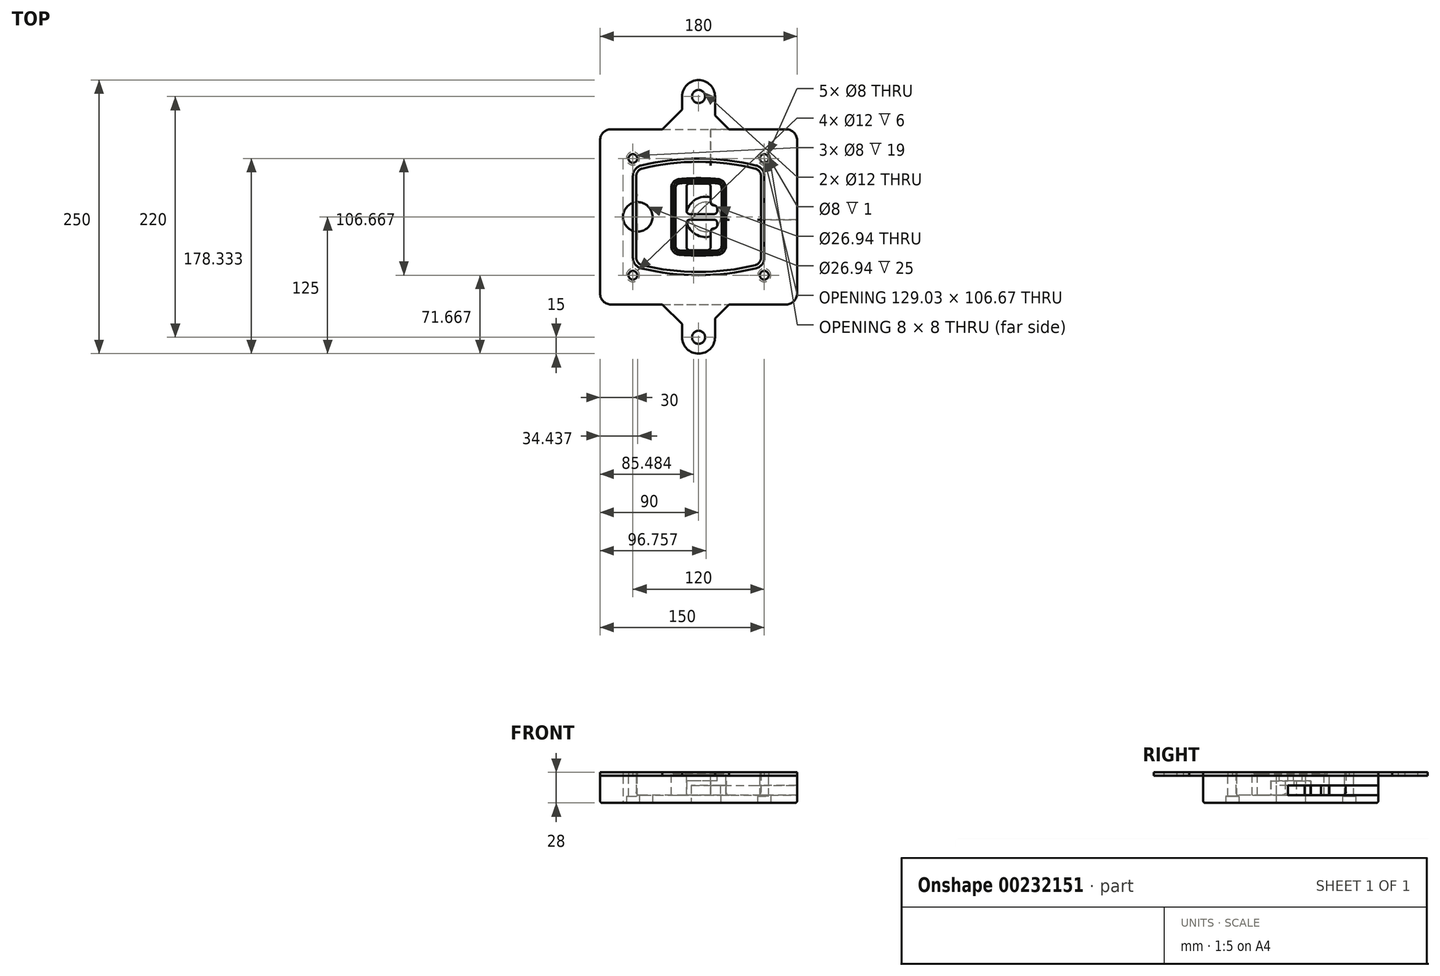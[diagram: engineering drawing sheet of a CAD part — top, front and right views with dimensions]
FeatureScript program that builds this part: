
annotation { "Feature Type Name" : "Feature", "Feature Type Description" : "" }
export const myFeature = defineFeature(function(context is Context, id is Id, definition is map)
    precondition{}
    {
        {
            var Q0;
            Q0=qCreatedBy(makeId("Top.planeOp"),FACE);
            var sketch = newSketch(context, id + "F0", { "sketchPlane" : qUnion([Q0])});
            skPoint(sketch, "E0.rect.middle", {"position": v(0, 0) * mm});
            skLineSegment(sketch, "E1.bottom", {"start": v(-80, -80) * mm, "end": v(80, -80) * mm});
            skLineSegment(sketch, "E1.top", {"start": v(-80, 80) * mm, "end": v(80, 80) * mm});
            skLineSegment(sketch, "E1.left", {"start": v(-90, -70) * mm, "end": v(-90, 70) * mm});
            skLineSegment(sketch, "E1.right", {"start": v(90, -70) * mm, "end": v(90, 70) * mm});
            skLineSegment(sketch, "E2", {"start": v(-90, 80) * mm, "end": v(90, -80) * mm, "construction": true});
            skLineSegment(sketch, "E3", {"start": v(90, 80) * mm, "end": v(-90, -80) * mm, "construction": true});
            skCircle(sketch, "E4", {"center": v(-60, 53.33) * mm, "radius": 4 * mm});
            skCircle(sketch, "E5", {"center": v(60, 53.33) * mm, "radius": 4 * mm});
            skCircle(sketch, "E6", {"center": v(60, -53.33) * mm, "radius": 4 * mm});
            skCircle(sketch, "E7", {"center": v(-60, -53.33) * mm, "radius": 4 * mm});
            skLineSegment(sketch, "E8", {"start": v(-60, 53.33) * mm, "end": v(60, 53.33) * mm, "construction": true});
            skLineSegment(sketch, "E9", {"start": v(60, 53.33) * mm, "end": v(60, -53.33) * mm, "construction": true});
            skLineSegment(sketch, "E10", {"start": v(60, -53.33) * mm, "end": v(-60, -53.33) * mm, "construction": true});
            skLineSegment(sketch, "E11", {"start": v(-60, -53.33) * mm, "end": v(-60, 53.33) * mm, "construction": true});
            skLineSegment(sketch, "E12", {"start": v(-60, 37.3) * mm, "end": v(-60, -37.3) * mm});
            skLineSegment(sketch, "E13", {"start": v(60, 37.3) * mm, "end": v(60, -37.3) * mm});
            skArc(sketch, "E14", {"start": v(52.38, 47.01) * mm, "mid": v(0, 53.33) * mm, "end": v(-52.38, 47.01) * mm});
            skArc(sketch, "E15", {"start": v(-52.38, -47.01) * mm, "mid": v(0, -53.33) * mm, "end": v(52.38, -47.01) * mm});
            skLineSegment(sketch, "E16", {"start": v(-60, 0) * mm, "end": v(60, 0) * mm, "construction": true});
            skPoint(sketch, "E17.visualSharp", {"position": v(-60, -45) * mm});
            skArc(sketch, "E17.filletArc", {"start": v(-60, -37.3) * mm, "mid": v(-57.87, -43.47) * mm, "end": v(-52.38, -47.01) * mm});
            skPoint(sketch, "E18.visualSharp", {"position": v(-60, 45) * mm});
            skArc(sketch, "E18.filletArc", {"start": v(-52.38, 47.01) * mm, "mid": v(-57.87, 43.47) * mm, "end": v(-60, 37.3) * mm});
            skPoint(sketch, "E19.visualSharp", {"position": v(60, 45) * mm});
            skArc(sketch, "E19.filletArc", {"start": v(60, 37.3) * mm, "mid": v(57.87, 43.47) * mm, "end": v(52.38, 47.01) * mm});
            skPoint(sketch, "E20.visualSharp", {"position": v(60, -45) * mm});
            skArc(sketch, "E20.filletArc", {"start": v(52.38, -47.01) * mm, "mid": v(57.87, -43.47) * mm, "end": v(60, -37.3) * mm});
            skPoint(sketch, "E21.visualSharp", {"position": v(-90, 80) * mm});
            skArc(sketch, "E21.filletArc", {"start": v(-80, 80) * mm, "mid": v(-87.07, 77.07) * mm, "end": v(-90, 70) * mm});
            skPoint(sketch, "E22.visualSharp", {"position": v(90, 80) * mm});
            skArc(sketch, "E22.filletArc", {"start": v(90, 70) * mm, "mid": v(87.07, 77.07) * mm, "end": v(80, 80) * mm});
            skPoint(sketch, "E23.visualSharp", {"position": v(90, -80) * mm});
            skArc(sketch, "E23.filletArc", {"start": v(80, -80) * mm, "mid": v(87.07, -77.07) * mm, "end": v(90, -70) * mm});
            skPoint(sketch, "E24.visualSharp", {"position": v(-90, -80) * mm});
            skArc(sketch, "E24.filletArc", {"start": v(-90, -70) * mm, "mid": v(-87.07, -77.07) * mm, "end": v(-80, -80) * mm});
            skArc(sketch, "E25.0", {"start": v(57, 37.3) * mm, "mid": v(55.5, 41.62) * mm, "end": v(51.67, 44.1) * mm});
            skLineSegment(sketch, "E25.1", {"start": v(57, 37.3) * mm, "end": v(57, -37.3) * mm});
            skArc(sketch, "E25.2", {"start": v(51.67, -44.1) * mm, "mid": v(55.5, -41.62) * mm, "end": v(57, -37.3) * mm});
            skArc(sketch, "E25.3", {"start": v(-51.67, -44.1) * mm, "mid": v(0, -50.33) * mm, "end": v(51.67, -44.1) * mm});
            skArc(sketch, "E25.4", {"start": v(-57, -37.3) * mm, "mid": v(-55.5, -41.62) * mm, "end": v(-51.67, -44.1) * mm});
            skArc(sketch, "E25.5", {"start": v(51.67, 44.1) * mm, "mid": v(0, 50.33) * mm, "end": v(-51.67, 44.1) * mm});
            skLineSegment(sketch, "E25.6", {"start": v(-57, 37.3) * mm, "end": v(-57, -37.3) * mm});
            skArc(sketch, "E25.7", {"start": v(-51.67, 44.1) * mm, "mid": v(-55.5, 41.62) * mm, "end": v(-57, 37.3) * mm});
            skArc(sketch, "E26.0", {"start": v(-53.33, 50.9) * mm, "mid": v(-61.01, 45.94) * mm, "end": v(-64, 37.3) * mm});
            skArc(sketch, "E26.1", {"start": v(53.33, 50.9) * mm, "mid": v(0, 57.33) * mm, "end": v(-53.33, 50.9) * mm});
            skArc(sketch, "E26.2", {"start": v(64, 37.3) * mm, "mid": v(61.01, 45.94) * mm, "end": v(53.33, 50.9) * mm});
            skLineSegment(sketch, "E26.3", {"start": v(64, 37.3) * mm, "end": v(64, -37.3) * mm});
            skArc(sketch, "E26.4", {"start": v(53.33, -50.9) * mm, "mid": v(61.01, -45.94) * mm, "end": v(64, -37.3) * mm});
            skLineSegment(sketch, "E26.5", {"start": v(-64, 37.3) * mm, "end": v(-64, -37.3) * mm});
            skArc(sketch, "E26.6", {"start": v(-53.33, -50.9) * mm, "mid": v(0, -57.33) * mm, "end": v(53.33, -50.9) * mm});
            skArc(sketch, "E26.7", {"start": v(-64, -37.3) * mm, "mid": v(-61.01, -45.94) * mm, "end": v(-53.33, -50.9) * mm});
            skSolve(sketch);
        }
        {
            var Q0;
            Q0=makeQuery(id+"F0.imprint","IMPRINT",FACE,{"disambiguationData":[TD([[makeQuery(id+"F0.imprint","IMPRINT",EDGE,{"derivedFrom":sQuery(id+"F0.wireOp",EDGE,"E1.bottom")}),1.0]])]});
            var Q1;
            Q1=makeQuery(id+"F0.imprint","IMPRINT",FACE,{"disambiguationData":[TD([[makeQuery(id+"F0.imprint","IMPRINT",EDGE,{"derivedFrom":sQuery(id+"F0.wireOp",EDGE,"E12")}),1.0]])]});
            var Q2;
            Q2=makeQuery(id+"F0.imprint","IMPRINT",FACE,{"disambiguationData":[TD([[makeQuery(id+"F0.imprint","IMPRINT",EDGE,{"derivedFrom":sQuery(id+"F0.wireOp",EDGE,"E25.0")}),1.0]])]});
            var Q3;
            Q3=makeQuery(id+"F0.imprint","IMPRINT",FACE,{"disambiguationData":[TD([[makeQuery(id+"F0.imprint","IMPRINT",EDGE,{"derivedFrom":sQuery(id+"F0.wireOp",EDGE,"E12")}),-1.0]])]});
            extrude(context, id + "F1", {"entities" : qUnion([Q0, Q1, Q2, Q3]), "oppositeDirection" : true, "depth" : 25 * mm});
        }
        {
            var Q0;
            Q0=makeQuery(id+"F0.imprint","IMPRINT",FACE,{"disambiguationData":[TD([[makeQuery(id+"F0.imprint","IMPRINT",EDGE,{"derivedFrom":sQuery(id+"F0.wireOp",EDGE,"E12")}),1.0]])]});
            extrude(context, id + "F2", {"entities" : qUnion([Q0]), "operationType" : NewBodyOperationType.ADD, "depth" : 3 * mm});
        }
        {
            var Q0;
            Q0=makeQuery(id+"F0.imprint","IMPRINT",FACE,{"disambiguationData":[TD([[makeQuery(id+"F0.imprint","IMPRINT",EDGE,{"derivedFrom":sQuery(id+"F0.wireOp",EDGE,"E25.0")}),1.0]])]});
            extrude(context, id + "F3", {"entities" : qUnion([Q0]), "operationType" : NewBodyOperationType.REMOVE, "oppositeDirection" : true, "depth" : 18 * mm});
        }
        {
            var Q0;
            Q0=makeQuery(id+"F2.opExtrude","CAP_FACE",FACE,{"disambiguationData":[OSD([sQuery(id+"F0.wireOp",EDGE,"E12"),sQuery(id+"F0.wireOp",EDGE,"E13"),sQuery(id+"F0.wireOp",EDGE,"E14"),sQuery(id+"F0.wireOp",EDGE,"E15"),sQuery(id+"F0.wireOp",EDGE,"E17.filletArc"),sQuery(id+"F0.wireOp",EDGE,"E18.filletArc"),sQuery(id+"F0.wireOp",EDGE,"E19.filletArc"),sQuery(id+"F0.wireOp",EDGE,"E20.filletArc"),sQuery(id+"F0.wireOp",EDGE,"E25.0"),sQuery(id+"F0.wireOp",EDGE,"E25.1"),sQuery(id+"F0.wireOp",EDGE,"E25.2"),sQuery(id+"F0.wireOp",EDGE,"E25.3"),sQuery(id+"F0.wireOp",EDGE,"E25.4"),sQuery(id+"F0.wireOp",EDGE,"E25.5"),sQuery(id+"F0.wireOp",EDGE,"E25.6"),sQuery(id+"F0.wireOp",EDGE,"E25.7")])],"isStart":false});
            var sketch = newSketch(context, id + "F4", { "sketchPlane" : qUnion([Q0])});
            skArc(sketch, "E27.0", {"start": v(-17.7, -34.56) * mm, "mid": v(0, -35.33) * mm, "end": v(17.7, -34.56) * mm});
            skArc(sketch, "E28.0", {"start": v(17.7, 34.56) * mm, "mid": v(0, 35.33) * mm, "end": v(-17.7, 34.56) * mm});
            skLineSegment(sketch, "E29", {"start": v(-25, 26.59) * mm, "end": v(-25, -26.59) * mm});
            skLineSegment(sketch, "E30", {"start": v(25, 26.59) * mm, "end": v(25, -26.59) * mm});
            skLineSegment(sketch, "E31", {"start": v(-25, 33.78) * mm, "end": v(25, 33.78) * mm, "construction": true});
            skLineSegment(sketch, "E32", {"start": v(-25, -33.78) * mm, "end": v(25, -33.78) * mm, "construction": true});
            skPoint(sketch, "E33.visualSharp", {"position": v(-25, 33.78) * mm});
            skArc(sketch, "E33.filletArc", {"start": v(-17.7, 34.56) * mm, "mid": v(-22.9, 32) * mm, "end": v(-25, 26.59) * mm});
            skPoint(sketch, "E34.visualSharp", {"position": v(25, 33.78) * mm});
            skArc(sketch, "E34.filletArc", {"start": v(25, 26.59) * mm, "mid": v(22.9, 32) * mm, "end": v(17.7, 34.56) * mm});
            skPoint(sketch, "E35.visualSharp", {"position": v(25, -33.78) * mm});
            skArc(sketch, "E35.filletArc", {"start": v(17.7, -34.56) * mm, "mid": v(22.9, -32) * mm, "end": v(25, -26.59) * mm});
            skPoint(sketch, "E36.visualSharp", {"position": v(-25, -33.78) * mm});
            skArc(sketch, "E36.filletArc", {"start": v(-25, -26.59) * mm, "mid": v(-22.9, -32) * mm, "end": v(-17.7, -34.56) * mm});
            skArc(sketch, "E37.0", {"start": v(51.67, 44.1) * mm, "mid": v(0, 50.33) * mm, "end": v(-51.67, 44.1) * mm});
            skArc(sketch, "E37.1", {"start": v(-51.67, 44.1) * mm, "mid": v(-55.5, 41.62) * mm, "end": v(-57, 37.3) * mm});
            skLineSegment(sketch, "E37.2", {"start": v(-57, 37.3) * mm, "end": v(-57, -37.3) * mm});
            skArc(sketch, "E37.3", {"start": v(-57, -37.3) * mm, "mid": v(-55.5, -41.62) * mm, "end": v(-51.67, -44.1) * mm});
            skArc(sketch, "E37.4", {"start": v(-51.67, -44.1) * mm, "mid": v(0, -50.33) * mm, "end": v(51.67, -44.1) * mm});
            skArc(sketch, "E37.5", {"start": v(51.67, -44.1) * mm, "mid": v(55.5, -41.62) * mm, "end": v(57, -37.3) * mm});
            skLineSegment(sketch, "E37.6", {"start": v(57, 37.3) * mm, "end": v(57, -37.3) * mm});
            skArc(sketch, "E37.7", {"start": v(57, 37.3) * mm, "mid": v(55.5, 41.62) * mm, "end": v(51.67, 44.1) * mm});
            skLineSegment(sketch, "E38.0", {"start": v(23, 26.59) * mm, "end": v(23, -26.59) * mm});
            skArc(sketch, "E38.1", {"start": v(17.53, -32.56) * mm, "mid": v(21.42, -30.64) * mm, "end": v(23, -26.59) * mm});
            skArc(sketch, "E38.2", {"start": v(-17.53, -32.56) * mm, "mid": v(0, -33.33) * mm, "end": v(17.53, -32.56) * mm});
            skArc(sketch, "E38.3", {"start": v(-23, -26.59) * mm, "mid": v(-21.42, -30.64) * mm, "end": v(-17.53, -32.56) * mm});
            skLineSegment(sketch, "E38.4", {"start": v(-23, 26.59) * mm, "end": v(-23, -26.59) * mm});
            skArc(sketch, "E38.5", {"start": v(23, 26.59) * mm, "mid": v(21.42, 30.64) * mm, "end": v(17.53, 32.56) * mm});
            skArc(sketch, "E38.6", {"start": v(-17.53, 32.56) * mm, "mid": v(-21.42, 30.64) * mm, "end": v(-23, 26.59) * mm});
            skArc(sketch, "E38.7", {"start": v(17.53, 32.56) * mm, "mid": v(0, 33.33) * mm, "end": v(-17.53, 32.56) * mm});
            skArc(sketch, "E39.0", {"start": v(21, 26.59) * mm, "mid": v(19.95, 29.29) * mm, "end": v(17.35, 30.57) * mm});
            skLineSegment(sketch, "E39.1", {"start": v(21, 26.59) * mm, "end": v(21, -26.59) * mm});
            skArc(sketch, "E39.2", {"start": v(17.35, -30.57) * mm, "mid": v(19.95, -29.29) * mm, "end": v(21, -26.59) * mm});
            skArc(sketch, "E39.3", {"start": v(-17.35, -30.57) * mm, "mid": v(0, -31.33) * mm, "end": v(17.35, -30.57) * mm});
            skArc(sketch, "E39.4", {"start": v(-21, -26.59) * mm, "mid": v(-19.95, -29.29) * mm, "end": v(-17.35, -30.57) * mm});
            skArc(sketch, "E39.5", {"start": v(17.35, 30.57) * mm, "mid": v(0, 31.33) * mm, "end": v(-17.35, 30.57) * mm});
            skLineSegment(sketch, "E39.6", {"start": v(-21, 26.59) * mm, "end": v(-21, -26.59) * mm});
            skArc(sketch, "E39.7", {"start": v(-17.35, 30.57) * mm, "mid": v(-19.95, 29.29) * mm, "end": v(-21, 26.59) * mm});
            skLineSegment(sketch, "E40", {"start": v(-25, 0) * mm, "end": v(25, 0) * mm, "construction": true});
            skLineSegment(sketch, "E41", {"start": v(-11, 5.5) * mm, "end": v(-11, 27.5) * mm});
            skLineSegment(sketch, "E42", {"start": v(-8, 30.5) * mm, "end": v(8, 30.5) * mm});
            skLineSegment(sketch, "E43", {"start": v(11, 27.5) * mm, "end": v(11, 13.5) * mm});
            skLineSegment(sketch, "E44", {"start": v(14, 10.5) * mm, "end": v(14, 10.5) * mm});
            skLineSegment(sketch, "E45", {"start": v(17, 7.5) * mm, "end": v(17, 5.5) * mm});
            skLineSegment(sketch, "E46", {"start": v(14, 2.5) * mm, "end": v(-8, 2.5) * mm});
            skPoint(sketch, "E47.visualSharp", {"position": v(-11, 30.5) * mm});
            skArc(sketch, "E47.filletArc", {"start": v(-8, 30.5) * mm, "mid": v(-10.12, 29.62) * mm, "end": v(-11, 27.5) * mm});
            skPoint(sketch, "E48.visualSharp", {"position": v(11, 30.5) * mm});
            skArc(sketch, "E48.filletArc", {"start": v(11, 27.5) * mm, "mid": v(10.12, 29.62) * mm, "end": v(8, 30.5) * mm});
            skPoint(sketch, "E49.visualSharp", {"position": v(11, 10.5) * mm});
            skArc(sketch, "E49.filletArc", {"start": v(11, 13.5) * mm, "mid": v(11.88, 11.38) * mm, "end": v(14, 10.5) * mm});
            skPoint(sketch, "E50.visualSharp", {"position": v(17, 10.5) * mm});
            skArc(sketch, "E50.filletArc", {"start": v(17, 7.5) * mm, "mid": v(16.12, 9.62) * mm, "end": v(14, 10.5) * mm});
            skPoint(sketch, "E51.visualSharp", {"position": v(17, 2.5) * mm});
            skArc(sketch, "E51.filletArc", {"start": v(14, 2.5) * mm, "mid": v(16.12, 3.38) * mm, "end": v(17, 5.5) * mm});
            skPoint(sketch, "E52.visualSharp", {"position": v(-11, 2.5) * mm});
            skArc(sketch, "E52.filletArc", {"start": v(-11, 5.5) * mm, "mid": v(-10.12, 3.38) * mm, "end": v(-8, 2.5) * mm});
            skLineSegment(sketch, "E53.0.MirrorCS", {"start": v(14, -2.5) * mm, "end": v(-8, -2.5) * mm});
            skArc(sketch, "E54.0.MirrorCS", {"start": v(-11, -5.5) * mm, "mid": v(-10.12, -3.38) * mm, "end": v(-8, -2.5) * mm});
            skLineSegment(sketch, "E55.0.MirrorCS", {"start": v(-11, -5.5) * mm, "end": v(-11, -27.5) * mm});
            skArc(sketch, "E56.0.MirrorCS", {"start": v(-8, -30.5) * mm, "mid": v(-10.12, -29.62) * mm, "end": v(-11, -27.5) * mm});
            skLineSegment(sketch, "E57.0.MirrorCS", {"start": v(-8, -30.5) * mm, "end": v(8, -30.5) * mm});
            skArc(sketch, "E58.0.MirrorCS", {"start": v(11, -27.5) * mm, "mid": v(10.12, -29.62) * mm, "end": v(8, -30.5) * mm});
            skLineSegment(sketch, "E59.0.MirrorCS", {"start": v(11, -27.5) * mm, "end": v(11, -13.5) * mm});
            skArc(sketch, "E60.0.MirrorCS", {"start": v(11, -13.5) * mm, "mid": v(11.88, -11.38) * mm, "end": v(14, -10.5) * mm});
            skArc(sketch, "E61.0.MirrorCS", {"start": v(17, -7.5) * mm, "mid": v(16.12, -9.62) * mm, "end": v(14, -10.5) * mm});
            skLineSegment(sketch, "E62.0.MirrorCS", {"start": v(17, -7.5) * mm, "end": v(17, -5.5) * mm});
            skArc(sketch, "E63.0.MirrorCS", {"start": v(14, -2.5) * mm, "mid": v(16.12, -3.38) * mm, "end": v(17, -5.5) * mm});
            skSolve(sketch);
        }
        {
            var Q0;
            Q0=makeQuery(id+"F4.imprint","IMPRINT",FACE,{"disambiguationData":[TD([[makeQuery(id+"F4.imprint","IMPRINT",EDGE,{"derivedFrom":sQuery(id+"F4.wireOp",EDGE,"E27.0")}),1.0]])]});
            var Q1;
            Q1=makeQuery(id+"F4.imprint","IMPRINT",FACE,{"disambiguationData":[TD([[makeQuery(id+"F4.imprint","IMPRINT",EDGE,{"derivedFrom":sQuery(id+"F4.wireOp",EDGE,"E38.0")}),-1.0]])]});
            var Q2;
            Q2=makeQuery(id+"F4.imprint","IMPRINT",FACE,{"disambiguationData":[TD([[makeQuery(id+"F4.imprint","IMPRINT",EDGE,{"derivedFrom":sQuery(id+"F4.wireOp",EDGE,"E39.0")}),1.0]])]});
            extrude(context, id + "F5", {"entities" : qUnion([Q0, Q1, Q2]), "operationType" : NewBodyOperationType.ADD, "endBound" : BoundingType.UP_TO_NEXT, "oppositeDirection" : true, "depth" : 25 * mm});
        }
        {
            var Q0;
            Q0=makeQuery(id+"F4.imprint","IMPRINT",FACE,{"disambiguationData":[TD([[makeQuery(id+"F4.imprint","IMPRINT",EDGE,{"derivedFrom":sQuery(id+"F4.wireOp",EDGE,"E38.0")}),-1.0]])]});
            extrude(context, id + "F6", {"entities" : qUnion([Q0]), "operationType" : NewBodyOperationType.REMOVE, "oppositeDirection" : true, "depth" : 2 * mm});
        }
        {
            var Q0;
            Q0=makeQuery(id+"F1.opExtrude","CAP_FACE",FACE,{"disambiguationData":[OSD([sQuery(id+"F0.wireOp",EDGE,"E1.bottom"),sQuery(id+"F0.wireOp",EDGE,"E1.top"),sQuery(id+"F0.wireOp",EDGE,"E1.left"),sQuery(id+"F0.wireOp",EDGE,"E1.right"),sQuery(id+"F0.wireOp",EDGE,"E4"),sQuery(id+"F0.wireOp",EDGE,"E5"),sQuery(id+"F0.wireOp",EDGE,"E6"),sQuery(id+"F0.wireOp",EDGE,"E7"),sQuery(id+"F0.wireOp",EDGE,"E21.filletArc"),sQuery(id+"F0.wireOp",EDGE,"E22.filletArc"),sQuery(id+"F0.wireOp",EDGE,"E23.filletArc"),sQuery(id+"F0.wireOp",EDGE,"E24.filletArc")])],"isStart":false});
            var sketch = newSketch(context, id + "F7", { "sketchPlane" : qUnion([Q0])});
            skCircle(sketch, "E64", {"center": v(6.76, 0) * mm, "radius": 13.47 * mm});
            skCircle(sketch, "E65", {"center": v(-55.56, 0) * mm, "radius": 13.47 * mm});
            skLineSegment(sketch, "E66", {"start": v(90, 0) * mm, "end": v(-90, 0) * mm});
            skCircle(sketch, "E67", {"center": v(6.76, 0) * mm, "radius": 18.47 * mm});
            skCircle(sketch, "E68", {"center": v(60, -53.33) * mm, "radius": 6 * mm});
            skCircle(sketch, "E69", {"center": v(-60, -53.33) * mm, "radius": 6 * mm});
            skCircle(sketch, "E70", {"center": v(-60, 53.33) * mm, "radius": 6 * mm});
            skCircle(sketch, "E71", {"center": v(60, 53.33) * mm, "radius": 6 * mm});
            skSolve(sketch);
        }
        {
            var Q0;
            {var subQ1=sQuery(id+"F7.wireOp",EDGE,"E66");var subQ4=sQuery(id+"F7.wireOp",EDGE,"E64");var subQ6=makeQuery(id+"F7.imprint","INTERSECT",VERTEX,{"disambiguationData":[OD(0.0)],"derivedFrom":[subQ4,subQ1]});Q0=makeQuery(id+"F7.imprint","IMPRINT",FACE,{"disambiguationData":[TD([[makeQuery(id+"F7.imprint","IMPRINT",EDGE,{"disambiguationData":[TD([[subQ6,-1.0]])],"derivedFrom":subQ4}),-1.0]])]});}
            var Q1;
            {var subQ0=sQuery(id+"F7.wireOp",EDGE,"E66");var subQ1=sQuery(id+"F7.wireOp",EDGE,"E64");var subQ3=makeQuery(id+"F7.imprint","INTERSECT",VERTEX,{"disambiguationData":[OD(0.0)],"derivedFrom":[subQ1,subQ0]});Q1=makeQuery(id+"F7.imprint","IMPRINT",FACE,{"disambiguationData":[TD([[makeQuery(id+"F7.imprint","IMPRINT",EDGE,{"disambiguationData":[TD([[subQ3,-1.0]])],"derivedFrom":subQ1}),1.0]])]});}
            var Q2;
            {var subQ0=sQuery(id+"F7.wireOp",EDGE,"E66");var subQ1=sQuery(id+"F7.wireOp",EDGE,"E64");var subQ3=makeQuery(id+"F7.imprint","INTERSECT",VERTEX,{"disambiguationData":[OD(0.0)],"derivedFrom":[subQ1,subQ0]});Q2=makeQuery(id+"F7.imprint","IMPRINT",FACE,{"disambiguationData":[TD([[makeQuery(id+"F7.imprint","IMPRINT",EDGE,{"disambiguationData":[TD([[subQ3,1.0]])],"derivedFrom":subQ1}),1.0]])]});}
            var Q3;
            {var subQ1=sQuery(id+"F7.wireOp",EDGE,"E66");var subQ4=sQuery(id+"F7.wireOp",EDGE,"E64");var subQ6=makeQuery(id+"F7.imprint","INTERSECT",VERTEX,{"disambiguationData":[OD(0.0)],"derivedFrom":[subQ4,subQ1]});Q3=makeQuery(id+"F7.imprint","IMPRINT",FACE,{"disambiguationData":[TD([[makeQuery(id+"F7.imprint","IMPRINT",EDGE,{"disambiguationData":[TD([[subQ6,1.0]])],"derivedFrom":subQ4}),-1.0]])]});}
            extrude(context, id + "F8", {"entities" : qUnion([Q0, Q1, Q2, Q3]), "operationType" : NewBodyOperationType.ADD, "oppositeDirection" : true, "depth" : 20 * mm});
        }
        {
            var Q0;
            {var subQ0=sQuery(id+"F7.wireOp",EDGE,"E66");var subQ1=sQuery(id+"F7.wireOp",EDGE,"E64");var subQ3=makeQuery(id+"F7.imprint","INTERSECT",VERTEX,{"disambiguationData":[OD(0.0)],"derivedFrom":[subQ1,subQ0]});Q0=makeQuery(id+"F7.imprint","IMPRINT",FACE,{"disambiguationData":[TD([[makeQuery(id+"F7.imprint","IMPRINT",EDGE,{"disambiguationData":[TD([[subQ3,-1.0]])],"derivedFrom":subQ1}),1.0]])]});}
            var Q1;
            {var subQ0=sQuery(id+"F7.wireOp",EDGE,"E66");var subQ1=sQuery(id+"F7.wireOp",EDGE,"E64");var subQ3=makeQuery(id+"F7.imprint","INTERSECT",VERTEX,{"disambiguationData":[OD(0.0)],"derivedFrom":[subQ1,subQ0]});Q1=makeQuery(id+"F7.imprint","IMPRINT",FACE,{"disambiguationData":[TD([[makeQuery(id+"F7.imprint","IMPRINT",EDGE,{"disambiguationData":[TD([[subQ3,1.0]])],"derivedFrom":subQ1}),1.0]])]});}
            extrude(context, id + "F9", {"entities" : qUnion([Q0, Q1]), "operationType" : NewBodyOperationType.REMOVE, "oppositeDirection" : true, "depth" : 16 * mm});
        }
        {
            var Q0;
            {var subQ0=sQuery(id+"F7.wireOp",EDGE,"E66");var subQ1=sQuery(id+"F7.wireOp",EDGE,"E65");var subQ3=makeQuery(id+"F7.imprint","INTERSECT",VERTEX,{"disambiguationData":[OD(0.0)],"derivedFrom":[subQ1,subQ0]});Q0=makeQuery(id+"F7.imprint","IMPRINT",FACE,{"disambiguationData":[TD([[makeQuery(id+"F7.imprint","IMPRINT",EDGE,{"disambiguationData":[TD([[subQ3,-1.0]])],"derivedFrom":subQ1}),1.0]])]});}
            var Q1;
            {var subQ0=sQuery(id+"F7.wireOp",EDGE,"E66");var subQ1=sQuery(id+"F7.wireOp",EDGE,"E65");var subQ3=makeQuery(id+"F7.imprint","INTERSECT",VERTEX,{"disambiguationData":[OD(0.0)],"derivedFrom":[subQ1,subQ0]});Q1=makeQuery(id+"F7.imprint","IMPRINT",FACE,{"disambiguationData":[TD([[makeQuery(id+"F7.imprint","IMPRINT",EDGE,{"disambiguationData":[TD([[subQ3,1.0]])],"derivedFrom":subQ1}),1.0]])]});}
            extrude(context, id + "F10", {"entities" : qUnion([Q0, Q1]), "operationType" : NewBodyOperationType.REMOVE, "oppositeDirection" : true, "depth" : 25 * mm});
        }
        {
            var Q0;
            Q0=makeQuery(id+"F7.imprint","IMPRINT",FACE,{"disambiguationData":[TD([[makeQuery(id+"F7.imprint","IMPRINT",EDGE,{"derivedFrom":sQuery(id+"F7.wireOp",EDGE,"E68")}),1.0]])]});
            var Q1;
            Q1=makeQuery(id+"F7.imprint","IMPRINT",FACE,{"disambiguationData":[TD([[makeQuery(id+"F7.imprint","IMPRINT",EDGE,{"derivedFrom":makeQuery(id+"F1.opExtrude","CAP_EDGE",EDGE,{"disambiguationData":[OSD([sQuery(id+"F0.wireOp",EDGE,"E5")])],"isStart":false})}),-1.0]])]});
            var Q2;
            Q2=makeQuery(id+"F7.imprint","IMPRINT",FACE,{"disambiguationData":[TD([[makeQuery(id+"F7.imprint","IMPRINT",EDGE,{"derivedFrom":sQuery(id+"F7.wireOp",EDGE,"E69")}),1.0]])]});
            var Q3;
            Q3=makeQuery(id+"F7.imprint","IMPRINT",FACE,{"disambiguationData":[TD([[makeQuery(id+"F7.imprint","IMPRINT",EDGE,{"derivedFrom":makeQuery(id+"F1.opExtrude","CAP_EDGE",EDGE,{"disambiguationData":[OSD([sQuery(id+"F0.wireOp",EDGE,"E4")])],"isStart":false})}),-1.0]])]});
            var Q4;
            Q4=makeQuery(id+"F7.imprint","IMPRINT",FACE,{"disambiguationData":[TD([[makeQuery(id+"F7.imprint","IMPRINT",EDGE,{"derivedFrom":sQuery(id+"F7.wireOp",EDGE,"E70")}),1.0]])]});
            var Q5;
            Q5=makeQuery(id+"F7.imprint","IMPRINT",FACE,{"disambiguationData":[TD([[makeQuery(id+"F7.imprint","IMPRINT",EDGE,{"derivedFrom":makeQuery(id+"F1.opExtrude","CAP_EDGE",EDGE,{"disambiguationData":[OSD([sQuery(id+"F0.wireOp",EDGE,"E7")])],"isStart":false})}),-1.0]])]});
            var Q6;
            Q6=makeQuery(id+"F7.imprint","IMPRINT",FACE,{"disambiguationData":[TD([[makeQuery(id+"F7.imprint","IMPRINT",EDGE,{"derivedFrom":sQuery(id+"F7.wireOp",EDGE,"E71")}),1.0]])]});
            var Q7;
            Q7=makeQuery(id+"F7.imprint","IMPRINT",FACE,{"disambiguationData":[TD([[makeQuery(id+"F7.imprint","IMPRINT",EDGE,{"derivedFrom":makeQuery(id+"F1.opExtrude","CAP_EDGE",EDGE,{"disambiguationData":[OSD([sQuery(id+"F0.wireOp",EDGE,"E6")])],"isStart":false})}),-1.0]])]});
            extrude(context, id + "F11", {"entities" : qUnion([Q0, Q1, Q2, Q3, Q4, Q5, Q6, Q7]), "operationType" : NewBodyOperationType.REMOVE, "oppositeDirection" : true, "depth" : 6 * mm});
        }
        {
            var Q0;
            Q0=makeQuery(id+"F9.boolean.opBoolean","COPY",FACE,{"derivedFrom":makeQuery(id+"F9.opExtrude","CAP_FACE",FACE,{"disambiguationData":[OSD([sQuery(id+"F7.wireOp",EDGE,"E64")])],"isStart":false})});
            var sketch = newSketch(context, id + "F12", { "sketchPlane" : qUnion([Q0])});
            skArc(sketch, "E72.0", {"start": v(11, -88.19) * mm, "mid": v(97.1, -83.6) * mm, "end": v(92.5, 2.5) * mm});
            skLineSegment(sketch, "E72.1", {"start": v(11, -17.97) * mm, "end": v(11, -17.97) * mm});
            skLineSegment(sketch, "E73", {"start": v(92.5, -105.13) * mm, "end": v(102.3, -105.13) * mm});
            skLineSegment(sketch, "E74.0", {"start": v(92.5, 2.5) * mm, "end": v(14, 2.5) * mm});
            skArc(sketch, "E74.1", {"start": v(14, 2.5) * mm, "mid": v(16.12, 3.38) * mm, "end": v(17, 5.5) * mm});
            skLineSegment(sketch, "E74.2", {"start": v(17, 7.5) * mm, "end": v(17, 5.5) * mm});
            skArc(sketch, "E74.3", {"start": v(17, 7.5) * mm, "mid": v(16.12, 9.62) * mm, "end": v(14, 10.5) * mm});
            skArc(sketch, "E74.4", {"start": v(11, 13.5) * mm, "mid": v(11.88, 11.38) * mm, "end": v(14, 10.5) * mm});
            skLineSegment(sketch, "E74.5", {"start": v(11, 13.5) * mm, "end": v(11, -88.19) * mm});
            skLineSegment(sketch, "E74.7", {"start": v(92.5, -2.5) * mm, "end": v(14, -2.5) * mm});
            skArc(sketch, "E74.8", {"start": v(14, -2.5) * mm, "mid": v(16.12, -3.38) * mm, "end": v(17, -5.5) * mm});
            skLineSegment(sketch, "E74.9", {"start": v(17, -7.5) * mm, "end": v(17, -5.5) * mm});
            skArc(sketch, "E74.10", {"start": v(17, -7.5) * mm, "mid": v(16.12, -9.62) * mm, "end": v(14, -10.5) * mm});
            skArc(sketch, "E74.11", {"start": v(11, -13.5) * mm, "mid": v(11.88, -11.38) * mm, "end": v(14, -10.5) * mm});
            skLineSegment(sketch, "E74.12", {"start": v(11, -17.97) * mm, "end": v(11, -13.5) * mm});
            skPoint(sketch, "E75.orphan", {"position": v(11, -27.5) * mm});
            skPoint(sketch, "E76.orphan", {"position": v(-8, -2.5) * mm});
            skPoint(sketch, "E77.orphan", {"position": v(-8, 2.5) * mm});
            skPoint(sketch, "E78.orphan", {"position": v(11, 27.5) * mm});
            skSolve(sketch);
        }
        {
            var Q0;
            {var subQ7=sQuery(id+"F12.wireOp",EDGE,"E72.0");var subQ14=sQuery(id+"F12.wireOp",EDGE,"E72.1");var subQ16=sQuery(id+"F12.wireOp",EDGE,"E74.1");var subQ18=sQuery(id+"F12.wireOp",EDGE,"E74.8");Q0=qUnion([makeQuery(id+"F12.imprint","IMPRINT",FACE,{"disambiguationData":[TD([[makeQuery(id+"F12.imprint","IMPRINT",EDGE,{"derivedFrom":subQ7}),1.0]])]}),makeQuery(id+"F12.imprint","IMPRINT",FACE,{"disambiguationData":[TD([[makeQuery(id+"F12.imprint","IMPRINT",EDGE,{"derivedFrom":subQ14}),1.0]])]}),makeQuery(id+"F12.imprint","IMPRINT",FACE,{"disambiguationData":[TD([[makeQuery(id+"F12.imprint","IMPRINT",EDGE,{"derivedFrom":subQ16}),1.0]])]}),makeQuery(id+"F12.imprint","IMPRINT",FACE,{"disambiguationData":[TD([[makeQuery(id+"F12.imprint","IMPRINT",EDGE,{"derivedFrom":subQ18}),-1.0]])]})]);}
            var Q1;
            Q1=makeQuery(id+"F5.boolean.opBoolean","SPLIT",FACE,{"disambiguationData":[TD([makeQuery(id+"F5.opExtrude","SWEPT_FACE",FACE,{"disambiguationData":[OSD([sQuery(id+"F4.wireOp",EDGE,"E41")])]})])],"derivedFrom":makeQuery(id+"F3.boolean.opBoolean","COPY",FACE,{"derivedFrom":makeQuery(id+"F3.opExtrude","CAP_FACE",FACE,{"disambiguationData":[OSD([sQuery(id+"F0.wireOp",EDGE,"E25.0"),sQuery(id+"F0.wireOp",EDGE,"E25.1"),sQuery(id+"F0.wireOp",EDGE,"E25.2"),sQuery(id+"F0.wireOp",EDGE,"E25.3"),sQuery(id+"F0.wireOp",EDGE,"E25.4"),sQuery(id+"F0.wireOp",EDGE,"E25.5"),sQuery(id+"F0.wireOp",EDGE,"E25.6"),sQuery(id+"F0.wireOp",EDGE,"E25.7")])],"isStart":false})})});
            extrude(context, id + "F13", {"entities" : qUnion([Q0]), "operationType" : NewBodyOperationType.REMOVE, "endBound" : BoundingType.UP_TO_SURFACE, "endBoundEntityFace" : qUnion([Q1]), "depth" : 25 * mm});
        }
        {
            var Q0;
            Q0=makeQuery(id+"F3.boolean.opBoolean","COPY",EDGE,{"derivedFrom":makeQuery(id+"F3.opExtrude","CAP_EDGE",EDGE,{"disambiguationData":[OSD([sQuery(id+"F0.wireOp",EDGE,"E25.6")])],"isStart":false})});
            var Q1;
            Q1=makeQuery(id+"F8.boolean.opBoolean","INTERSECT",EDGE,{"derivedFrom":[makeQuery(id+"F5.opExtrude","SWEPT_FACE",FACE,{"disambiguationData":[OSD([sQuery(id+"F4.wireOp",EDGE,"E30")])]}),makeQuery(id+"F8.opExtrude","CAP_FACE",FACE,{"disambiguationData":[OSD([sQuery(id+"F7.wireOp",EDGE,"E67")])],"isStart":false})]});
            var Q2;
            Q2=makeQuery(id+"F8.boolean.opBoolean","INTERSECT",EDGE,{"disambiguationData":[OD(1.0)],"derivedFrom":[makeQuery(id+"F5.opExtrude","SWEPT_FACE",FACE,{"disambiguationData":[OSD([sQuery(id+"F4.wireOp",EDGE,"E30")])]}),makeQuery(id+"F8.opExtrude","SWEPT_FACE",FACE,{"disambiguationData":[OSD([sQuery(id+"F7.wireOp",EDGE,"E67")])]})]});
            var Q3;
            {var subQ0=makeQuery(id+"F3.boolean.opBoolean","COPY",FACE,{"derivedFrom":makeQuery(id+"F3.opExtrude","CAP_FACE",FACE,{"disambiguationData":[OSD([sQuery(id+"F0.wireOp",EDGE,"E25.0"),sQuery(id+"F0.wireOp",EDGE,"E25.1"),sQuery(id+"F0.wireOp",EDGE,"E25.2"),sQuery(id+"F0.wireOp",EDGE,"E25.3"),sQuery(id+"F0.wireOp",EDGE,"E25.4"),sQuery(id+"F0.wireOp",EDGE,"E25.5"),sQuery(id+"F0.wireOp",EDGE,"E25.6"),sQuery(id+"F0.wireOp",EDGE,"E25.7")])],"isStart":false})});var subQ1=sQuery(id+"F4.wireOp",EDGE,"E30");Q3=makeQuery(id+"F8.boolean.opBoolean","SPLIT",EDGE,{"disambiguationData":[TD([makeQuery(id+"F5.opExtrude","SWEPT_FACE",FACE,{"disambiguationData":[OSD([sQuery(id+"F4.wireOp",EDGE,"E35.filletArc")])]})])],"derivedFrom":makeQuery(id+"F5.opExtrude","TWEAK_EDGE",EDGE,{"derivedFrom":[subQ0,makeQuery(id+"F4.imprint","IMPRINT",EDGE,{"derivedFrom":subQ1})]})});}
            var Q4;
            {var subQ0=sQuery(id+"F0.wireOp",EDGE,"E25.0");var subQ1=sQuery(id+"F0.wireOp",EDGE,"E25.1");var subQ2=sQuery(id+"F0.wireOp",EDGE,"E25.2");var subQ3=sQuery(id+"F0.wireOp",EDGE,"E25.3");var subQ4=sQuery(id+"F0.wireOp",EDGE,"E25.4");var subQ5=sQuery(id+"F0.wireOp",EDGE,"E25.5");var subQ6=sQuery(id+"F0.wireOp",EDGE,"E25.6");var subQ7=sQuery(id+"F0.wireOp",EDGE,"E25.7");Q4=makeQuery(id+"F8.boolean.opBoolean","INTERSECT",EDGE,{"derivedFrom":[makeQuery(id+"F5.boolean.opBoolean","SPLIT",FACE,{"disambiguationData":[TD([makeQuery(id+"F2.opExtrude","SWEPT_FACE",FACE,{"disambiguationData":[OSD([subQ0])]})])],"derivedFrom":makeQuery(id+"F3.boolean.opBoolean","COPY",FACE,{"derivedFrom":makeQuery(id+"F3.opExtrude","CAP_FACE",FACE,{"disambiguationData":[OSD([subQ0,subQ1,subQ2,subQ3,subQ4,subQ5,subQ6,subQ7])],"isStart":false})})}),makeQuery(id+"F8.opExtrude","SWEPT_FACE",FACE,{"disambiguationData":[OSD([sQuery(id+"F7.wireOp",EDGE,"E67")])]})]});}
            var Q5;
            Q5=makeQuery(id+"F8.boolean.opBoolean","INTERSECT",EDGE,{"disambiguationData":[OD(0.0)],"derivedFrom":[makeQuery(id+"F5.opExtrude","SWEPT_FACE",FACE,{"disambiguationData":[OSD([sQuery(id+"F4.wireOp",EDGE,"E30")])]}),makeQuery(id+"F8.opExtrude","SWEPT_FACE",FACE,{"disambiguationData":[OSD([sQuery(id+"F7.wireOp",EDGE,"E67")])]})]});
            fillet(context, id + "F14", {"entities" : qUnion([Q0, Q1, Q2, Q3, Q4, Q5]), "radius" : 3 * mm, "tangentPropagation" : true, "allowEdgeOverflow" : false});
        }
        {
            var Q0;
            Q0=makeQuery(id+"F1.opExtrude","CAP_EDGE",EDGE,{"disambiguationData":[OSD([sQuery(id+"F0.wireOp",EDGE,"E1.bottom")])],"isStart":false});
            fillet(context, id + "F15", {"entities" : qUnion([Q0]), "radius" : 2 * mm, "tangentPropagation" : true, "allowEdgeOverflow" : false});
        }
        {
            var Q0;
            {var subQ0=sQuery(id+"F0.wireOp",EDGE,"E22.filletArc");var subQ1=sQuery(id+"F0.wireOp",EDGE,"E7");var subQ2=sQuery(id+"F0.wireOp",EDGE,"E6");var subQ3=sQuery(id+"F0.wireOp",EDGE,"E5");var subQ4=sQuery(id+"F0.wireOp",EDGE,"E4");var subQ5=sQuery(id+"F0.wireOp",EDGE,"E1.bottom");var subQ6=sQuery(id+"F0.wireOp",EDGE,"E21.filletArc");var subQ7=sQuery(id+"F0.wireOp",EDGE,"E1.top");var subQ8=sQuery(id+"F0.wireOp",EDGE,"E1.left");var subQ9=sQuery(id+"F0.wireOp",EDGE,"E1.right");var subQ10=sQuery(id+"F0.wireOp",EDGE,"E23.filletArc");var subQ11=sQuery(id+"F0.wireOp",EDGE,"E24.filletArc");Q0=makeQuery(id+"F2.boolean.opBoolean","SPLIT",FACE,{"disambiguationData":[TD([makeQuery(id+"F1.opExtrude","SWEPT_FACE",FACE,{"disambiguationData":[OSD([subQ5])]})])],"derivedFrom":makeQuery(id+"F1.opExtrude","CAP_FACE",FACE,{"disambiguationData":[OSD([subQ5,subQ7,subQ8,subQ9,subQ4,subQ3,subQ2,subQ1,subQ6,subQ0,subQ10,subQ11])],"isStart":true})});}
            var sketch = newSketch(context, id + "F16", { "sketchPlane" : qUnion([Q0])});
            skLineSegment(sketch, "E79", {"start": v(0, 80) * mm, "end": v(0, 110) * mm, "construction": true});
            skPoint(sketch, "E79.endSnap0", {"position": v(0, 80) * mm});
            skCircle(sketch, "E80", {"center": v(0, 110) * mm, "radius": 6 * mm});
            skLineSegment(sketch, "E81", {"start": v(-15, 110) * mm, "end": v(-15, 98) * mm});
            skLineSegment(sketch, "E82", {"start": v(15, 110) * mm, "end": v(15, 92.66) * mm});
            skLineSegment(sketch, "E83", {"start": v(15, 92.66) * mm, "end": v(27.66, 80) * mm});
            skArc(sketch, "E84", {"start": v(15, 110) * mm, "mid": v(0, 125) * mm, "end": v(-15, 110) * mm});
            skLineSegment(sketch, "E85", {"start": v(-15, 98) * mm, "end": v(-33, 80) * mm});
            skLineSegment(sketch, "E86", {"start": v(-90, 0) * mm, "end": v(90, 0) * mm, "construction": true});
            skLineSegment(sketch, "E87.MirrorCS", {"start": v(15, -92.66) * mm, "end": v(27.66, -80) * mm});
            skLineSegment(sketch, "E88.MirrorCS", {"start": v(15, -110) * mm, "end": v(15, -92.66) * mm});
            skArc(sketch, "E89.MirrorCS", {"start": v(15, -110) * mm, "mid": v(0, -125) * mm, "end": v(-15, -110) * mm});
            skLineSegment(sketch, "E90.MirrorCS", {"start": v(-15, -110) * mm, "end": v(-15, -98) * mm});
            skLineSegment(sketch, "E91.MirrorCS", {"start": v(-15, -98) * mm, "end": v(-33, -80) * mm});
            skLineSegment(sketch, "E92.MirrorCS", {"start": v(0, -80) * mm, "end": v(0, -110) * mm, "construction": true});
            skCircle(sketch, "E93.MirrorC", {"center": v(0, -110) * mm, "radius": 6 * mm});
            skSolve(sketch);
        }
        {
            var Q0;
            {var subQ0=sQuery(id+"F16.wireOp",EDGE,"E87.MirrorCS");Q0=makeQuery(id+"F16.imprint","IMPRINT",FACE,{"disambiguationData":[TD([[makeQuery(id+"F16.imprint","IMPRINT",EDGE,{"derivedFrom":subQ0}),1.0]])]});}
            var Q1;
            Q1=makeQuery(id+"F16.imprint","IMPRINT",FACE,{"disambiguationData":[TD([[makeQuery(id+"F16.imprint","IMPRINT",EDGE,{"derivedFrom":sQuery(id+"F16.wireOp",EDGE,"E80")}),-1.0]])]});
            var Q2;
            Q2=makeQuery(id+"F16.imprint","IMPRINT",FACE,{"disambiguationData":[TD([[makeQuery(id+"F16.imprint","IMPRINT",EDGE,{"derivedFrom":makeQuery(id+"F1.opExtrude","CAP_EDGE",EDGE,{"disambiguationData":[OSD([sQuery(id+"F0.wireOp",EDGE,"E1.left")])],"isStart":true})}),-1.0]])]});
            var Q3;
            Q3=makeQuery(id+"F2.opExtrude","CAP_FACE",FACE,{"disambiguationData":[OSD([sQuery(id+"F0.wireOp",EDGE,"E12"),sQuery(id+"F0.wireOp",EDGE,"E13"),sQuery(id+"F0.wireOp",EDGE,"E14"),sQuery(id+"F0.wireOp",EDGE,"E15"),sQuery(id+"F0.wireOp",EDGE,"E17.filletArc"),sQuery(id+"F0.wireOp",EDGE,"E18.filletArc"),sQuery(id+"F0.wireOp",EDGE,"E19.filletArc"),sQuery(id+"F0.wireOp",EDGE,"E20.filletArc"),sQuery(id+"F0.wireOp",EDGE,"E25.0"),sQuery(id+"F0.wireOp",EDGE,"E25.1"),sQuery(id+"F0.wireOp",EDGE,"E25.2"),sQuery(id+"F0.wireOp",EDGE,"E25.3"),sQuery(id+"F0.wireOp",EDGE,"E25.4"),sQuery(id+"F0.wireOp",EDGE,"E25.5"),sQuery(id+"F0.wireOp",EDGE,"E25.6"),sQuery(id+"F0.wireOp",EDGE,"E25.7")])],"isStart":false});
            var Q4;
            Q4=makeQuery(id+"F1.opExtrude","SWEPT_BODY",BODY,{"disambiguationData":[OSD([sQuery(id+"F0.wireOp",EDGE,"E1.bottom"),sQuery(id+"F0.wireOp",EDGE,"E1.top"),sQuery(id+"F0.wireOp",EDGE,"E1.left"),sQuery(id+"F0.wireOp",EDGE,"E1.right"),sQuery(id+"F0.wireOp",EDGE,"E4"),sQuery(id+"F0.wireOp",EDGE,"E5"),sQuery(id+"F0.wireOp",EDGE,"E6"),sQuery(id+"F0.wireOp",EDGE,"E7"),sQuery(id+"F0.wireOp",EDGE,"E21.filletArc"),sQuery(id+"F0.wireOp",EDGE,"E22.filletArc"),sQuery(id+"F0.wireOp",EDGE,"E23.filletArc"),sQuery(id+"F0.wireOp",EDGE,"E24.filletArc")])]});
            extrude(context, id + "F17", {"entities" : qUnion([Q0, Q1, Q2]), "endBound" : BoundingType.UP_TO_SURFACE, "endBoundEntityFace" : qUnion([Q3]), "endBoundEntityBody" : qUnion([Q4]), "depth" : 2.5 * mm});
        }
    });
